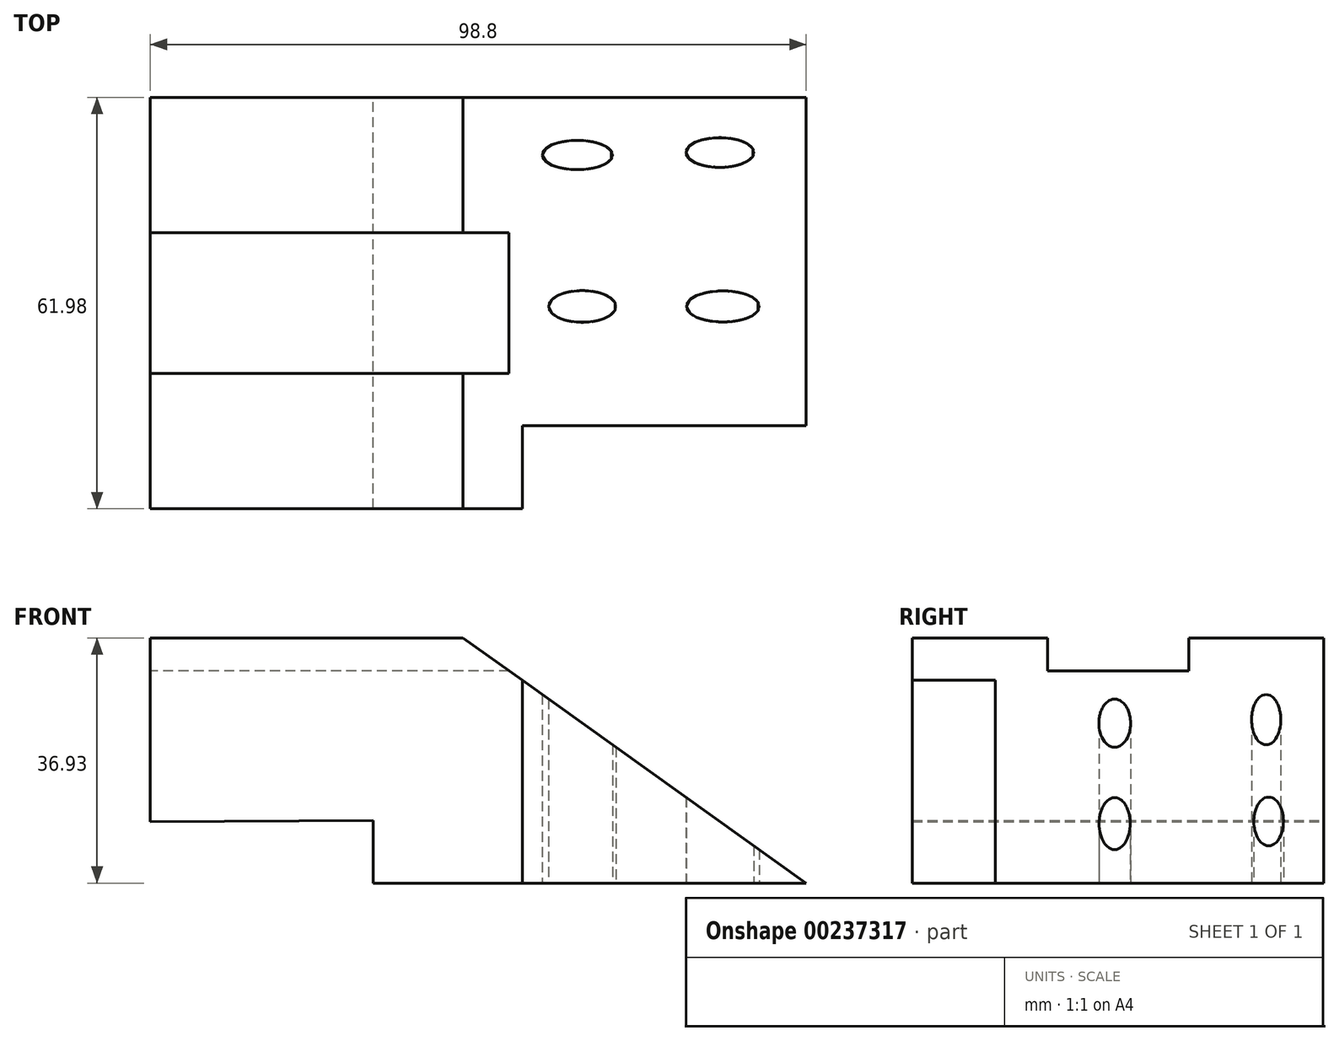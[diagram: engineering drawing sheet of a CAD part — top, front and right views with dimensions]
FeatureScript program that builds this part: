
annotation { "Feature Type Name" : "Feature", "Feature Type Description" : "" }
export const myFeature = defineFeature(function(context is Context, id is Id, definition is map)
    precondition{}
    {
        {
            var Q0;
            Q0=qCreatedBy(makeId("Front.planeOp"),FACE);
            var sketch = newSketch(context, id + "F0", { "sketchPlane" : qUnion([Q0])});
            skLineSegment(sketch, "E0", {"start": v(-51.5, 9.26) * mm, "end": v(-51.5, 36.93) * mm});
            skLineSegment(sketch, "E1", {"start": v(-51.5, 36.93) * mm, "end": v(-4.4, 36.93) * mm});
            skLineSegment(sketch, "E2", {"start": v(-4.4, 36.93) * mm, "end": v(47.3, 0) * mm});
            skLineSegment(sketch, "E3", {"start": v(47.3, 0) * mm, "end": v(-17.96, 0) * mm});
            skLineSegment(sketch, "E4", {"start": v(-17.96, 0) * mm, "end": v(-17.96, 9.44) * mm});
            skLineSegment(sketch, "E5", {"start": v(-17.96, 9.44) * mm, "end": v(-51.5, 9.26) * mm});
            skLineSegment(sketch, "E6", {"start": v(-39.23, 36.93) * mm, "end": v(-39.23, 41.7) * mm});
            skSolve(sketch);
        }
        {
            var Q0;
            {var subQ3=sQuery(id+"F0.wireOp",EDGE,"E0");Q0=makeQuery(id+"F0.imprint","IMPRINT",FACE,{"disambiguationData":[TD([[makeQuery(id+"F0.imprint","IMPRINT",EDGE,{"derivedFrom":subQ3}),-1.0]])]});}
            extrude(context, id + "F1", {"entities" : qUnion([Q0]), "depth" : 30.48 * mm, "hasSecondDirection" : true, "secondDirectionOppositeDirection" : true, "secondDirectionDepth" : 31.5 * mm});
        }
        {
            var Q0;
            Q0=makeQuery(id+"F1.opExtrude","SWEPT_FACE",FACE,{"disambiguationData":[OSD([sQuery(id+"F0.wireOp",EDGE,"E0")])]});
            var sketch = newSketch(context, id + "F2", { "sketchPlane" : qUnion([Q0])});
            skLineSegment(sketch, "E7.bottom", {"start": v(-11.14, 31.99) * mm, "end": v(10.12, 31.99) * mm});
            skLineSegment(sketch, "E7.top", {"start": v(-11.14, 41.88) * mm, "end": v(10.12, 41.88) * mm});
            skLineSegment(sketch, "E7.left", {"start": v(-11.14, 31.99) * mm, "end": v(-11.14, 41.88) * mm});
            skLineSegment(sketch, "E7.right", {"start": v(10.12, 31.99) * mm, "end": v(10.12, 41.88) * mm});
            skPoint(sketch, "E7.middle", {"position": v(-0.5, 36.93) * mm});
            skSolve(sketch);
        }
        {
            var Q0;
            {var subQ0=sQuery(id+"F2.wireOp",EDGE,"E7.bottom");Q0=makeQuery(id+"F2.imprint","IMPRINT",FACE,{"disambiguationData":[TD([[makeQuery(id+"F2.imprint","IMPRINT",EDGE,{"derivedFrom":subQ0}),1.0]])]});}
            extrude(context, id + "F3", {"entities" : qUnion([Q0]), "operationType" : NewBodyOperationType.REMOVE, "oppositeDirection" : true, "depth" : 62.23 * mm});
        }
        {
            var Q0;
            Q0=makeQuery(id+"F1.opExtrude","SWEPT_FACE",FACE,{"disambiguationData":[OSD([sQuery(id+"F0.wireOp",EDGE,"E3")])]});
            var sketch = newSketch(context, id + "F4", { "sketchPlane" : qUnion([Q0])});
            skLineSegment(sketch, "E8.bottom", {"start": v(47.3, 30.48) * mm, "end": v(4.52, 30.48) * mm});
            skLineSegment(sketch, "E8.top", {"start": v(47.3, 18) * mm, "end": v(4.52, 18) * mm});
            skLineSegment(sketch, "E8.left", {"start": v(47.3, 30.48) * mm, "end": v(47.3, 18) * mm});
            skLineSegment(sketch, "E8.right", {"start": v(4.52, 30.48) * mm, "end": v(4.52, 18) * mm});
            skSolve(sketch);
        }
        {
            var Q0;
            Q0=makeQuery(id+"F4.imprint","IMPRINT",FACE,{"disambiguationData":[TD([[makeQuery(id+"F4.imprint","IMPRINT",EDGE,{"derivedFrom":sQuery(id+"F4.wireOp",EDGE,"E8.bottom")}),1.0]])]});
            extrude(context, id + "F5", {"entities" : qUnion([Q0]), "operationType" : NewBodyOperationType.REMOVE, "oppositeDirection" : true, "depth" : 50.04 * mm});
        }
        {
            var Q0;
            Q0=makeQuery(id+"F1.opExtrude","SWEPT_FACE",FACE,{"disambiguationData":[OSD([sQuery(id+"F0.wireOp",EDGE,"E3")])]});
            var sketch = newSketch(context, id + "F6", { "sketchPlane" : qUnion([Q0])});
            skEllipse(sketch, "E9", {"center": v(34.75, 0) * mm, "majorRadius": 5.5 * mm, "minorRadius": 2.34 * mm, "majorAxis": v(-1, 0)});
            skEllipse(sketch, "E10", {"center": v(13.56, 0) * mm, "majorRadius": 5.08 * mm, "minorRadius": 2.39 * mm, "majorAxis": v(-1, 0)});
            skEllipse(sketch, "E11", {"center": v(12.83, -22.82) * mm, "majorRadius": 5.32 * mm, "minorRadius": 2.2 * mm, "majorAxis": v(-1, 0)});
            skEllipse(sketch, "E12", {"center": v(34.3, -23.2) * mm, "majorRadius": 5.13 * mm, "minorRadius": 2.24 * mm, "majorAxis": v(-1, 0)});
            skSolve(sketch);
        }
        {
            var Q0;
            Q0=makeQuery(id+"F6.imprint","IMPRINT",FACE,{"disambiguationData":[TD([[makeQuery(id+"F6.imprint","IMPRINT",EDGE,{"derivedFrom":sQuery(id+"F6.wireOp",EDGE,"E10")}),1.0]])]});
            var Q1;
            Q1=makeQuery(id+"F6.imprint","IMPRINT",FACE,{"disambiguationData":[TD([[makeQuery(id+"F6.imprint","IMPRINT",EDGE,{"derivedFrom":sQuery(id+"F6.wireOp",EDGE,"E11")}),1.0]])]});
            var Q2;
            Q2=makeQuery(id+"F6.imprint","IMPRINT",FACE,{"disambiguationData":[TD([[makeQuery(id+"F6.imprint","IMPRINT",EDGE,{"derivedFrom":sQuery(id+"F6.wireOp",EDGE,"E12")}),1.0]])]});
            var Q3;
            Q3=makeQuery(id+"F6.imprint","IMPRINT",FACE,{"disambiguationData":[TD([[makeQuery(id+"F6.imprint","IMPRINT",EDGE,{"derivedFrom":sQuery(id+"F6.wireOp",EDGE,"E9")}),1.0]])]});
            extrude(context, id + "F7", {"entities" : qUnion([Q0, Q1, Q2, Q3]), "operationType" : NewBodyOperationType.REMOVE, "oppositeDirection" : true, "depth" : 40.4 * mm});
        }
    });
